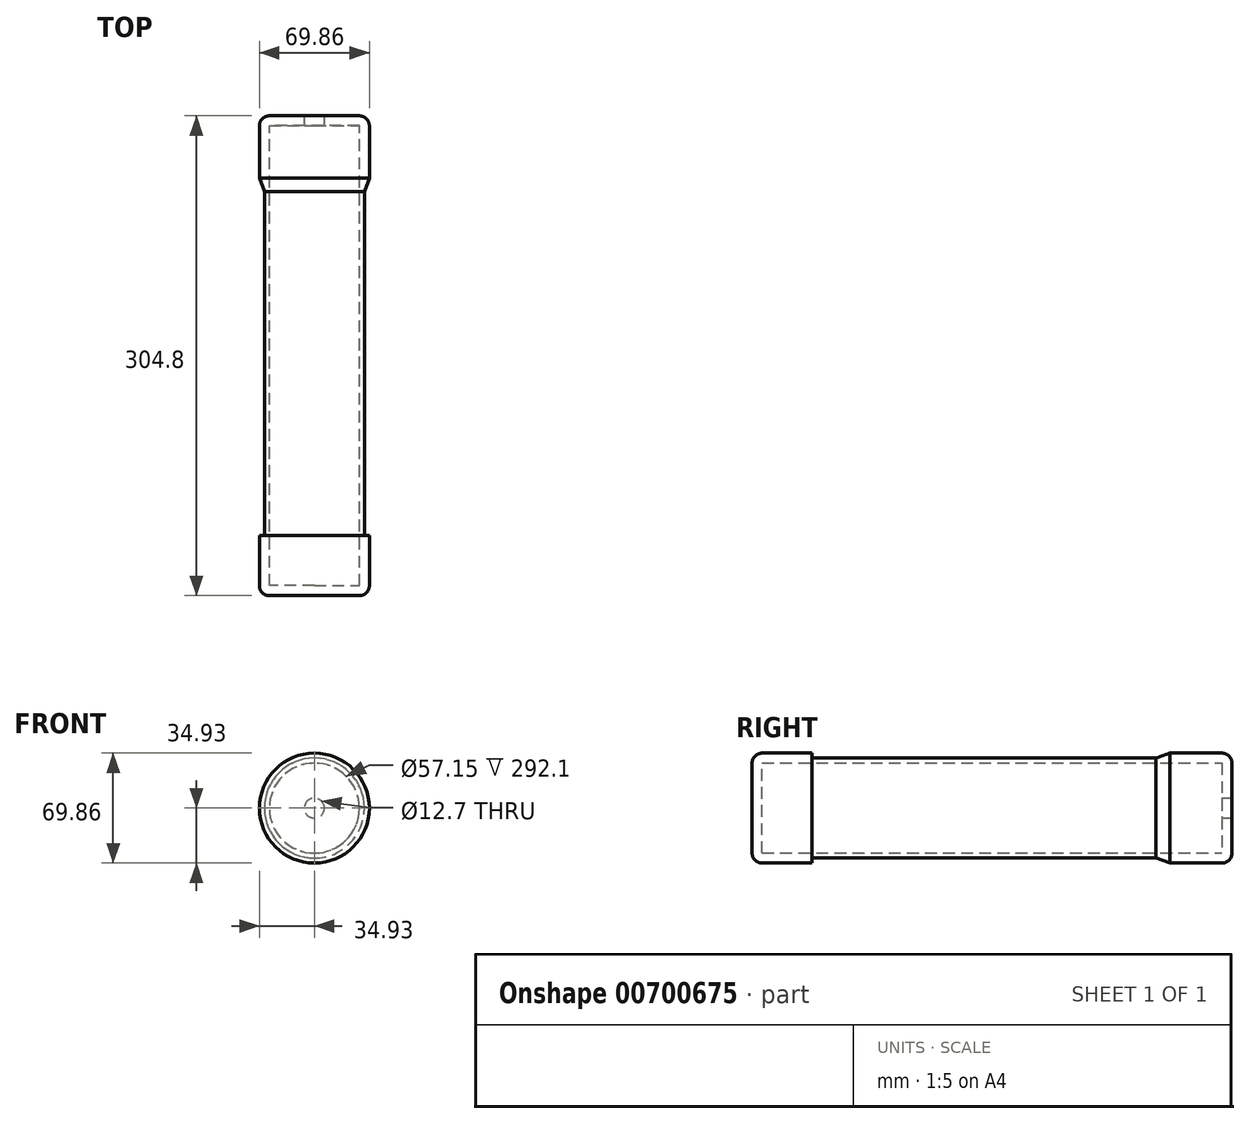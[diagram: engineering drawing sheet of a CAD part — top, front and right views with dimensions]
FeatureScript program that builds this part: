
annotation { "Feature Type Name" : "Feature", "Feature Type Description" : "" }
export const myFeature = defineFeature(function(context is Context, id is Id, definition is map)
    precondition{}
    {
        {
            var Q0;
            Q0=qCreatedBy(makeId("Front.planeOp"),FACE);
            var sketch = newSketch(context, id + "F0", { "sketchPlane" : qUnion([Q0])});
            skCircle(sketch, "E0", {"center": v(0, 0) * mm, "radius": 28.57 * mm});
            skCircle(sketch, "E1", {"center": v(0, 0) * mm, "radius": 34.92 * mm});
            skSolve(sketch);
        }
        {
            var Q0;
            Q0 = qSketchRegion(id + "F0", true);
            extrude(context, id + "F1", {"entities" : qUnion([Q0]), "depth" : 304.8 * mm, "offsetDistance" : 25.4 * mm});
        }
        {
            var Q0;
            Q0=makeQuery(id+"F1.opExtrude","CAP_FACE",FACE,{"disambiguationData":[OSD([sQuery(id+"F0.wireOp",EDGE,"E0"),sQuery(id+"F0.wireOp",EDGE,"E1")])],"isStart":false});
            var sketch = newSketch(context, id + "F2", { "sketchPlane" : qUnion([Q0])});
            skCircle(sketch, "E2.0", {"center": v(0, 0) * mm, "radius": 34.92 * mm});
            skSolve(sketch);
        }
        {
            var Q0;
            Q0 = qSketchRegion(id + "F2", true);
            extrude(context, id + "F3", {"entities" : qUnion([Q0]), "operationType" : NewBodyOperationType.ADD, "oppositeDirection" : true, "depth" : 6.35 * mm, "offsetDistance" : 25.4 * mm});
        }
        {
            var Q0;
            Q0=makeQuery(id+"F1.opExtrude","CAP_FACE",FACE,{"disambiguationData":[OSD([sQuery(id+"F0.wireOp",EDGE,"E0"),sQuery(id+"F0.wireOp",EDGE,"E1")])],"isStart":true});
            var sketch = newSketch(context, id + "F4", { "sketchPlane" : qUnion([Q0])});
            skCircle(sketch, "E3.0", {"center": v(0, 0) * mm, "radius": 34.92 * mm});
            skSolve(sketch);
        }
        {
            var Q0;
            Q0 = qSketchRegion(id + "F4", true);
            extrude(context, id + "F5", {"entities" : qUnion([Q0]), "operationType" : NewBodyOperationType.ADD, "oppositeDirection" : true, "depth" : 6.35 * mm, "offsetDistance" : 25.4 * mm});
        }
        {
            var Q0;
            Q0=makeQuery(id+"F1.opExtrude","CAP_EDGE",EDGE,{"disambiguationData":[OSD([sQuery(id+"F0.wireOp",EDGE,"E1")])],"isStart":true});
            fillet(context, id + "F6", {"entities" : qUnion([Q0]), "radius" : 6.35 * mm, "tangentPropagation" : true, "allowEdgeOverflow" : false});
        }
        {
            var Q0;
            Q0=makeQuery(id+"F1.opExtrude","CAP_EDGE",EDGE,{"disambiguationData":[OSD([sQuery(id+"F0.wireOp",EDGE,"E1")])],"isStart":false});
            fillet(context, id + "F7", {"entities" : qUnion([Q0]), "radius" : 6.35 * mm, "tangentPropagation" : true, "allowEdgeOverflow" : false});
        }
        {
            var Q0;
            Q0=qCreatedBy(makeId("Right.planeOp"),FACE);
            var sketch = newSketch(context, id + "F8", { "sketchPlane" : qUnion([Q0])});
            skLineSegment(sketch, "E4.bottom", {"start": v(-266.7, -31.75) * mm, "end": v(-38.1, -31.75) * mm});
            skLineSegment(sketch, "E4.top", {"start": v(-266.7, -34.93) * mm, "end": v(-38.1, -34.93) * mm});
            skLineSegment(sketch, "E4.left", {"start": v(-266.7, -31.75) * mm, "end": v(-266.7, -34.93) * mm});
            skLineSegment(sketch, "E4.right", {"start": v(-38.1, -31.75) * mm, "end": v(-38.1, -34.93) * mm});
            skPoint(sketch, "E5", {"position": v(-152.4, -34.92) * mm});
            skPoint(sketch, "E6", {"position": v(-152.4, -34.93) * mm});
            skSolve(sketch);
        }
        {
            var Q0;
            Q0 = qSketchRegion(id + "F8", true);
            var Q1;
            {var subQ0=sQuery(id+"F0.wireOp",EDGE,"E1");Q1=makeQuery(id+"F7.opFillet","BLEND_EDGE",EDGE,{"blendedFrom":[makeQuery(id+"F1.opExtrude","CAP_EDGE",EDGE,{"disambiguationData":[OSD([subQ0])],"isStart":false}),makeQuery(id+"F3.boolean.opBoolean","MERGE",FACE,{"derivedFrom":[makeQuery(id+"F1.opExtrude","CAP_FACE",FACE,{"disambiguationData":[OSD([sQuery(id+"F0.wireOp",EDGE,"E0"),subQ0])],"isStart":false}),makeQuery(id+"F3.opExtrude","CAP_FACE",FACE,{"disambiguationData":[OSD([sQuery(id+"F2.wireOp",EDGE,"E2.0")])],"isStart":true})]})],"blendedInto":[makeQuery(id+"F3.boolean.opBoolean","MERGE",FACE,{"derivedFrom":[makeQuery(id+"F1.opExtrude","CAP_FACE",FACE,{"disambiguationData":[OSD([sQuery(id+"F0.wireOp",EDGE,"E0"),subQ0])],"isStart":false}),makeQuery(id+"F3.opExtrude","CAP_FACE",FACE,{"disambiguationData":[OSD([sQuery(id+"F2.wireOp",EDGE,"E2.0")])],"isStart":true})]})]});}
            revolve(context, id + "F9", {"operationType" : NewBodyOperationType.REMOVE, "entities" : qUnion([Q0]), "axis" : qUnion([Q1]), "revolveType" : RevolveType.FULL, "oppositeDirection" : true});
        }
        {
            var Q0;
            Q0=makeQuery(id+"F9.boolean.opBoolean","COPY",EDGE,{"derivedFrom":makeQuery(id+"F9.opRevolve","SWEPT_EDGE",EDGE,{"disambiguationData":[OSD([sQuery(id+"F8.wireOp",EDGE,"E4.top"),sQuery(id+"F8.wireOp",EDGE,"E4.left")])]})});
            var Q1;
            Q1=makeQuery(id+"F9.boolean.opBoolean","COPY",EDGE,{"derivedFrom":makeQuery(id+"F9.opRevolve","SWEPT_EDGE",EDGE,{"disambiguationData":[OSD([sQuery(id+"F8.wireOp",EDGE,"E4.bottom"),sQuery(id+"F8.wireOp",EDGE,"E4.right")])]})});
            chamfer(context, id + "F10", {"entities" : qUnion([Q0, Q1]), "chamferType" : ChamferType.OFFSET_ANGLE, "width" : 10.16 * mm, "oppositeDirection" : false, "angle" : 20 * degree, "tangentPropagation" : true});
        }
        {
            var Q0;
            Q0=makeQuery(id+"F5.boolean.opBoolean","MERGE",FACE,{"derivedFrom":[makeQuery(id+"F1.opExtrude","CAP_FACE",FACE,{"disambiguationData":[OSD([sQuery(id+"F0.wireOp",EDGE,"E0"),sQuery(id+"F0.wireOp",EDGE,"E1")])],"isStart":true}),makeQuery(id+"F5.opExtrude","CAP_FACE",FACE,{"disambiguationData":[OSD([sQuery(id+"F4.wireOp",EDGE,"E3.0")])],"isStart":true})]});
            var sketch = newSketch(context, id + "F11", { "sketchPlane" : qUnion([Q0])});
            skCircle(sketch, "E7", {"center": v(0, 0) * mm, "radius": 6.35 * mm});
            skSolve(sketch);
        }
        {
            var Q0;
            Q0 = qSketchRegion(id + "F11", true);
            extrude(context, id + "F12", {"entities" : qUnion([Q0]), "operationType" : NewBodyOperationType.REMOVE, "oppositeDirection" : true, "depth" : 25.4 * mm, "offsetDistance" : 25.4 * mm});
        }
    });
